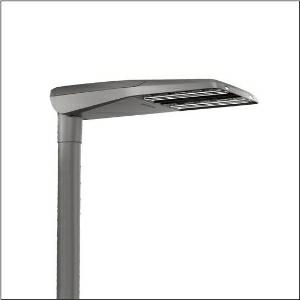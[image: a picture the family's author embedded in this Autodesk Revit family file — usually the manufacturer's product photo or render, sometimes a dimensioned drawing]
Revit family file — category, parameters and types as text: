
# Revit family: streetlight_sl_11_iq_midi___st1_2a_5xc3a61f08me_e1b3
name_source: partatom
category: Lighting Fixtures
units: mm (PartAtom-declared; Revit-internal decimal feet)

## family parameters
Cut with Voids When Loaded = No
Host = Face
Light Source = No
Part Type = Normal
Room Calculation Point = No
Round Connector Dimension = Use Diameter
Shared = No

## types (1)
- --- (1 x LED, 16120 lm, 123.9 W, 2700K)
    Apparent Load = 124 VA
    CIE Flux Codes = 32 70 96 100 100
    Color Rendering = 70
    Color Temperature = 2700K
    Default Elevation = 1800 mm
    Description = Streetlight SL 11 iQ midi, mast luminaire, primary light control with 3 zone facetted reflector, of plastic, silver coated, highly specular, primary optical cover: cover, of PMMA, transparent, light distribution: ST1.2a, light emission: direct distribution, primary light characteristic: asymmetric, installation type: post-top, side-entry, lamps: LED, High Power LED, rated values: 16.120lm | 123,9W | 130,1lm/W (begin service life); end service life: 16.120lm | 130,9W; at 50% lumin. flux: 8.060lm | 56,7W | 142,2lm/W, colour temperature: 2700K, colour rendering: CRI > 70, light colour: 727, light setting 1 begin service life: 100% | 16.120lm | 123,9W | 130,1lm/W | 2.700K, light setting 1 end service life: 130,9W, further light settings possible, control: Street-Remote, Auto-Match, Temp-Guard, Lumen-Switch, Night-Set, Smart-Wire, Light-Fading, Desk-Remote (wireless, voltage-free reading and setting of iQ features in the workshop via application-optimized NFC function/RFID function), optimised constant luminous flux control (CLO 2.0), with cable H07RN-F 3x 1.5mm², mains connection: 230..240V, AC, 50/60Hz, connection cable pre-assembled, cable length: 12,5m, luminaire housing, of diecast aluminium, powder-coated, SITECO metallic grey (DB 702S), please order mast flange separately, inclination adjustable without tools: 0°, 5°, 10°, 15° (post-top) | 0°, -5°, -10°, -15° (side-entry), sealing non-destructively replaceable, multi-level sealing system, length: 780mm, width: 376mm, height: 118mm, mast flange for spigot size: 42mm (side-entry): 5XC10008XM4, 60/48mm (side-entry/post-top): 5XC10108XM2, 76/60mm (side-entry/post-top): 5XC10108XM1, equipment: Power, protection rating (complete): IP66, insulation class (complete): insulation class II (safety insulation), certification: CE, ENEC, ENEC+, VDE, impact resistance: IK10, permissible operating ambient temperature for outdoor applications: -25..+50°C, standard-compliant lighting for roads and squares, Environmental Product Declaration (EPD) tested and certified by an independent institute, packaging unit: 1 piece

Light Distribution: ST1.2a
    Height = 118 mm
    Lamp = 1 x LED
    Lamp Light Flux = 16120 lm
    Lamp Power = 123.9 W
    Lamp count = 1
    Length = 780 mm
    Luminous efficacy = 130 lm/W
    Manufacturer = Siteco
    ModVariant = No
    Model = 5XC3A61F08ME
    Number of Poles = 1
    OnlyDefault = Yes
    Power Factor = 1
    Product Name = Streetlight SL 11 iQ midi | ST1.2a
    Product group = mast luminaire | pylon top
    ProductGroupID = 6100
    Protection Class = Protection class II
    Protection Degree = IP 66
    RLX_Detail_Level = 1
    RLX_Emergency_Light_Flux = 0 lm
    RLX_Emergency_Type = 0
    RLX_Emergency_Type_DB = No
    RlxData = <blob elided: 70949 chars, md5=0d34619c>
    Socket = socket
    Standby Power = 0 W
    System Light Flux = 16119 lm
    System Power = 124 W
    Type Comments = factory setting: luminous flux: 100 % | dim-lin: 254 | 554 mA
    Type Image = l_1005960.jpg
    URL = http://relux.com
    VarID = @adj_086035
    Voltage = 0 V
    Weight = 0.00 kg
    Width = 376 mm

## geometry (parser evidence)
native form markers: Blend x4, Sweep x10
no freeform markers — native parametric forms only
